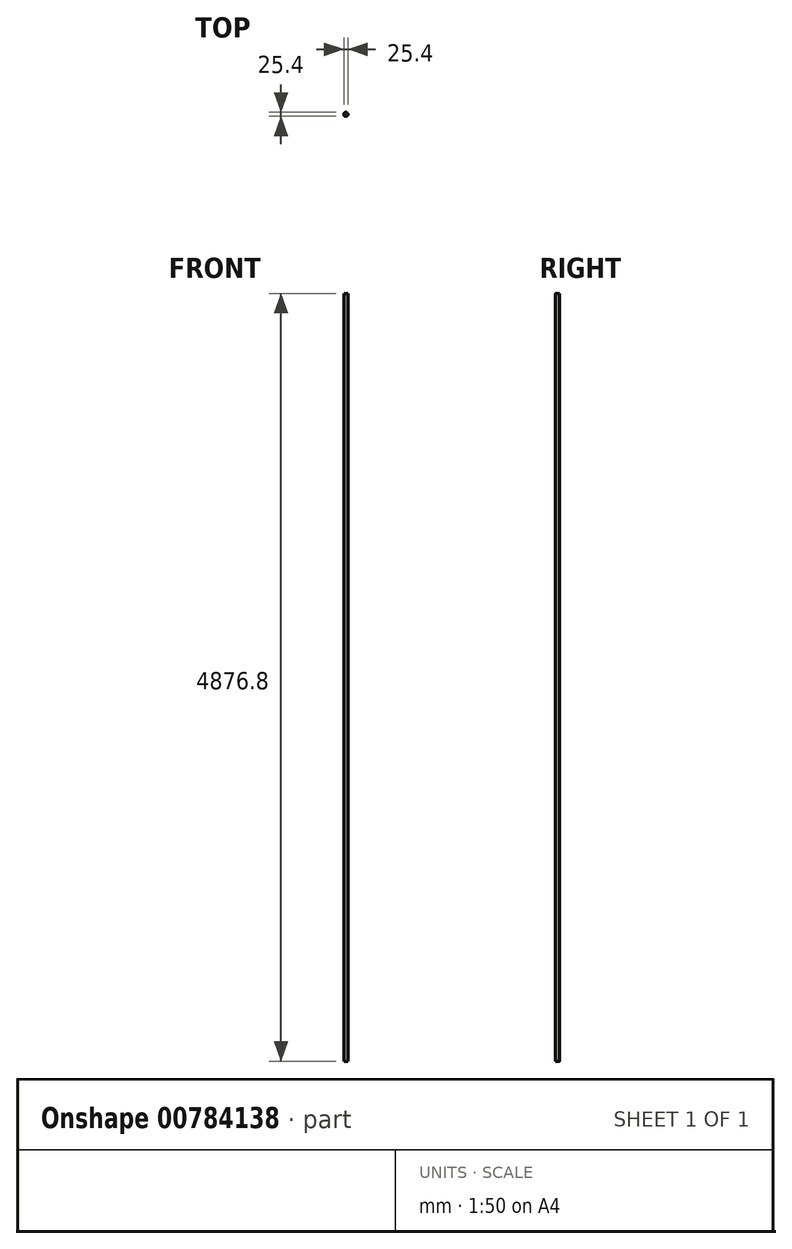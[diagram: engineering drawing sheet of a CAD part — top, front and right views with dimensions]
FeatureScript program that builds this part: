
annotation { "Feature Type Name" : "Feature", "Feature Type Description" : "" }
export const myFeature = defineFeature(function(context is Context, id is Id, definition is map)
    precondition{}
    {
        {
            var Q0;
            Q0=qCreatedBy(makeId("Top.planeOp"),FACE);
            var sketch = newSketch(context, id + "F0", { "sketchPlane" : qUnion([Q0])});
            skCircle(sketch, "E0", {"center": v(0, 0) * mm, "radius": 12.7 * mm});
            skSolve(sketch);
        }
        {
            var Q0;
            Q0=makeQuery(id+"F0.imprint","IMPRINT",FACE,{"disambiguationData":[TD([[makeQuery(id+"F0.imprint","IMPRINT",EDGE,{"derivedFrom":sQuery(id+"F0.wireOp",EDGE,"E0")}),1.0]])]});
            extrude(context, id + "F1", {"entities" : qUnion([Q0]), "depth" : 4876.8 * mm, "offsetDistance" : 25.4 * mm});
        }
    });
